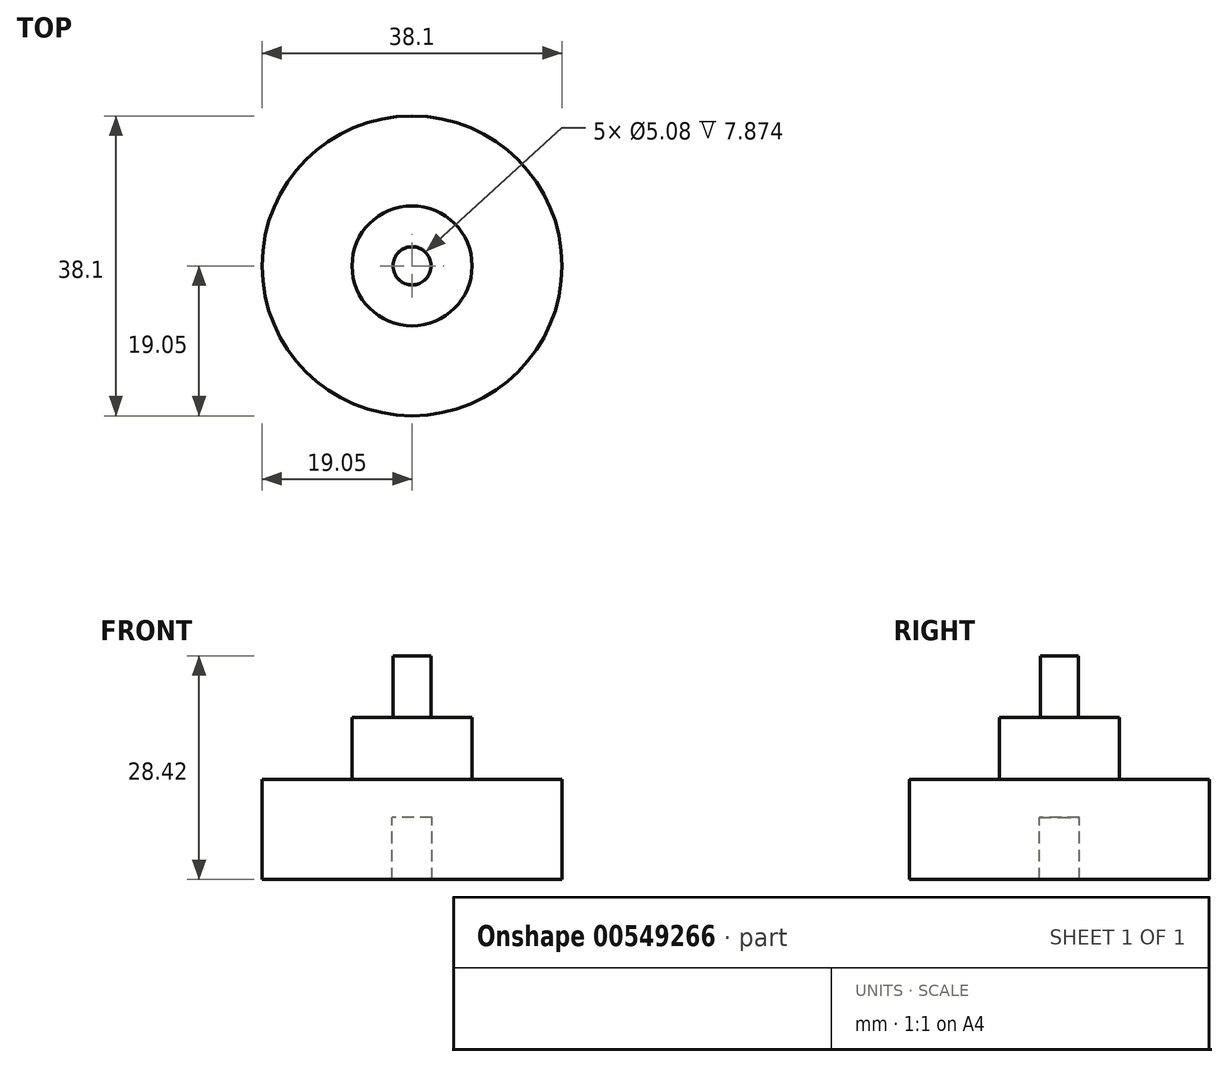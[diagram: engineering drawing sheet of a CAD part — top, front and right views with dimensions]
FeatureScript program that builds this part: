
annotation { "Feature Type Name" : "Feature", "Feature Type Description" : "" }
export const myFeature = defineFeature(function(context is Context, id is Id, definition is map)
    precondition{}
    {
        {
            var Q0;
            Q0=qCreatedBy(makeId("Front.planeOp"),FACE);
            var sketch = newSketch(context, id + "F0", { "sketchPlane" : qUnion([Q0])});
            skLineSegment(sketch, "E0", {"start": v(0, 0.24) * mm, "end": v(19.05, 0.24) * mm});
            skLineSegment(sketch, "E1", {"start": v(19.05, 0.24) * mm, "end": v(19.05, 12.94) * mm});
            skLineSegment(sketch, "E2", {"start": v(19.05, 12.94) * mm, "end": v(7.62, 12.94) * mm});
            skLineSegment(sketch, "E3", {"start": v(2.41, 20.81) * mm, "end": v(7.62, 20.81) * mm});
            skLineSegment(sketch, "E4", {"start": v(7.62, 20.81) * mm, "end": v(7.62, 12.94) * mm});
            skLineSegment(sketch, "E5", {"start": v(0, 28.66) * mm, "end": v(2.41, 28.66) * mm});
            skLineSegment(sketch, "E6", {"start": v(2.41, 28.66) * mm, "end": v(2.41, 20.81) * mm});
            skLineSegment(sketch, "E7", {"start": v(0, 0.24) * mm, "end": v(2.54, 0.24) * mm});
            skLineSegment(sketch, "E8", {"start": v(2.54, 0.24) * mm, "end": v(2.54, 8.11) * mm});
            skLineSegment(sketch, "E9", {"start": v(2.54, 8.11) * mm, "end": v(0, 8.11) * mm});
            skLineSegment(sketch, "E10", {"start": v(0, 28.66) * mm, "end": v(0, 8.11) * mm});
            skSolve(sketch);
        }
        {
            var Q0;
            Q0 = qSketchRegion(id + "F0", true);
            var Q1;
            Q1=sQuery(id+"F0.wireOp",EDGE,"E10");
            revolve(context, id + "F1", {"entities" : qUnion([Q0]), "axis" : qUnion([Q1]), "revolveType" : RevolveType.FULL});
        }
    });
